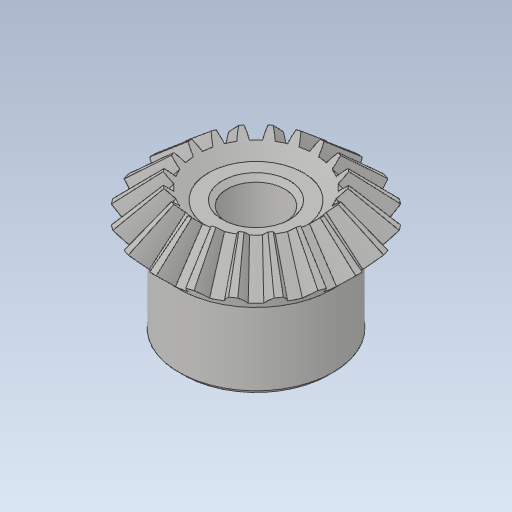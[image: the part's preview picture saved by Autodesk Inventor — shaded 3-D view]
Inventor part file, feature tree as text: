
AUTODESK INVENTOR PART (.ipt)
format: ipt  version: 2024 (Build 280153000, 153)  size: 567,296 bytes
history: native  units: mm
features: other x14, sketch x4, revolve x2, loft x1
ambient origin geometry x8: Origin, YZ Plane, XZ Plane, XY Plane, X Axis, Y Axis, Z Axis, Center Point
bodies: Solid1 (feature_tree)
feature tree (21):
  loft  "Loft1"
  revolve  "Revolution1"  Angle=360.0deg
  revolve  "Revolution2"  [1 undecoded]
  other  "IP2_XY"
  other  "IP2_YZ"
  other  "IP2_ZX"
  other  "IP2_X"
  other  "IP2_Y"
  other  "IP2_Z"
  other  "IP2_Center"
  other  "pm_XY"
  other  "pm_YZ"
  other  "pm_ZX"
  other  "pm_X"
  other  "pm_Y"
  other  "pm_Z"
  other  "pm_Center"
  sketch  "Sketch_4"  dims[d0=0.0mm d1=90.0deg d2=0.0mm d3=90.0deg]
  sketch  "Sketch_5"  dims[d4=360.0deg d5=360.0deg]
  sketch  "Sketch_6"
  sketch  "Sketch_7"
note: 1 required parameter value undecoded (feature->parameter linkage not recoverable at this tier; creation-order binding heuristic only, values carry confidence <= 0.55)
